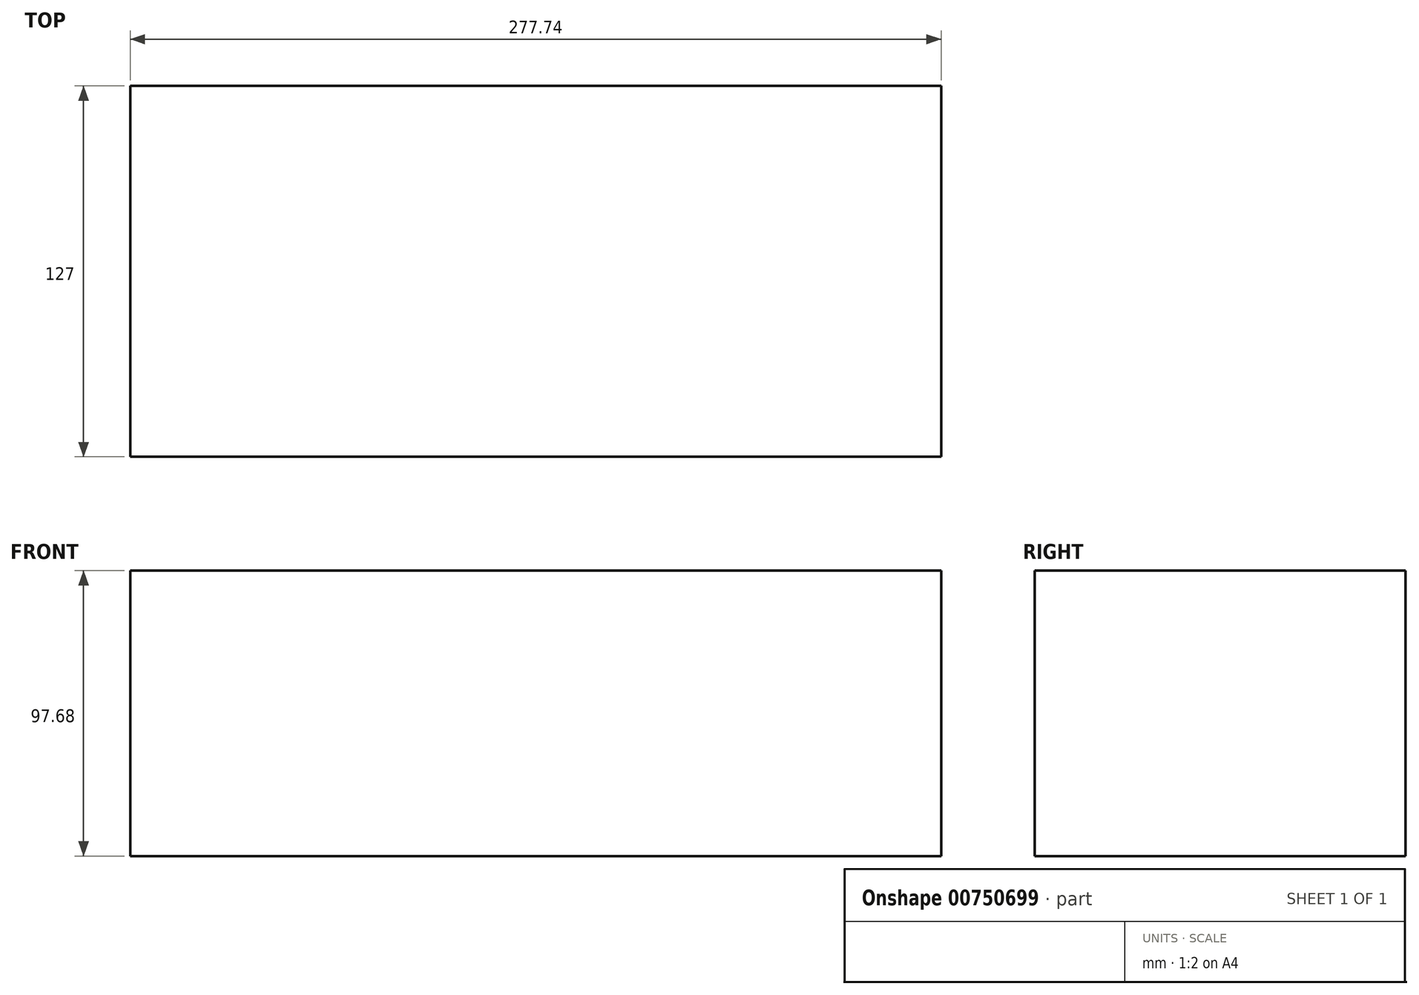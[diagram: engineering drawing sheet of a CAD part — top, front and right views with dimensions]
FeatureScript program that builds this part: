
annotation { "Feature Type Name" : "Feature", "Feature Type Description" : "" }
export const myFeature = defineFeature(function(context is Context, id is Id, definition is map)
    precondition{}
    {
        {
            var Q0;
            Q0=qCreatedBy(makeId("Front.planeOp"),FACE);
            var sketch = newSketch(context, id + "F0", { "sketchPlane" : qUnion([Q0])});
            skLineSegment(sketch, "E0.left", {"start": v(89.94, -120.6) * mm, "end": v(89.94, -120.6) * mm});
            skLineSegment(sketch, "E0.right", {"start": v(89.94, -120.6) * mm, "end": v(89.94, -120.6) * mm});
            skLineSegment(sketch, "E1.bottom", {"start": v(-97.22, 54.44) * mm, "end": v(41.9, 54.44) * mm});
            skLineSegment(sketch, "E1.top", {"start": v(-97.22, -35.02) * mm, "end": v(41.9, -35.02) * mm});
            skLineSegment(sketch, "E1.left", {"start": v(-97.22, 54.44) * mm, "end": v(-97.22, -35.02) * mm});
            skLineSegment(sketch, "E1.right", {"start": v(41.9, 54.44) * mm, "end": v(41.9, -35.02) * mm});
            skSolve(sketch);
        }
        {
            var Q0;
            Q0=qCreatedBy(makeId("Front.planeOp"),FACE);
            var sketch = newSketch(context, id + "F1", { "sketchPlane" : qUnion([Q0])});
            skLineSegment(sketch, "E2.bottom", {"start": v(-443, -189.76) * mm, "end": v(-165.25, -189.76) * mm});
            skLineSegment(sketch, "E2.top", {"start": v(-443, -287.44) * mm, "end": v(-165.25, -287.44) * mm});
            skLineSegment(sketch, "E2.left", {"start": v(-443, -189.76) * mm, "end": v(-443, -287.44) * mm});
            skLineSegment(sketch, "E2.right", {"start": v(-165.25, -189.76) * mm, "end": v(-165.25, -287.44) * mm});
            skSolve(sketch);
        }
        {
            var Q0;
            Q0=makeQuery(id+"F1.imprint","IMPRINT",FACE,{"disambiguationData":[TD([[makeQuery(id+"F1.imprint","IMPRINT",EDGE,{"derivedFrom":sQuery(id+"F1.wireOp",EDGE,"E2.bottom")}),-1.0]])]});
            extrude(context, id + "F2", {"entities" : qUnion([Q0]), "depth" : 127 * mm, "offsetDistance" : 25.4 * mm});
        }
    });
